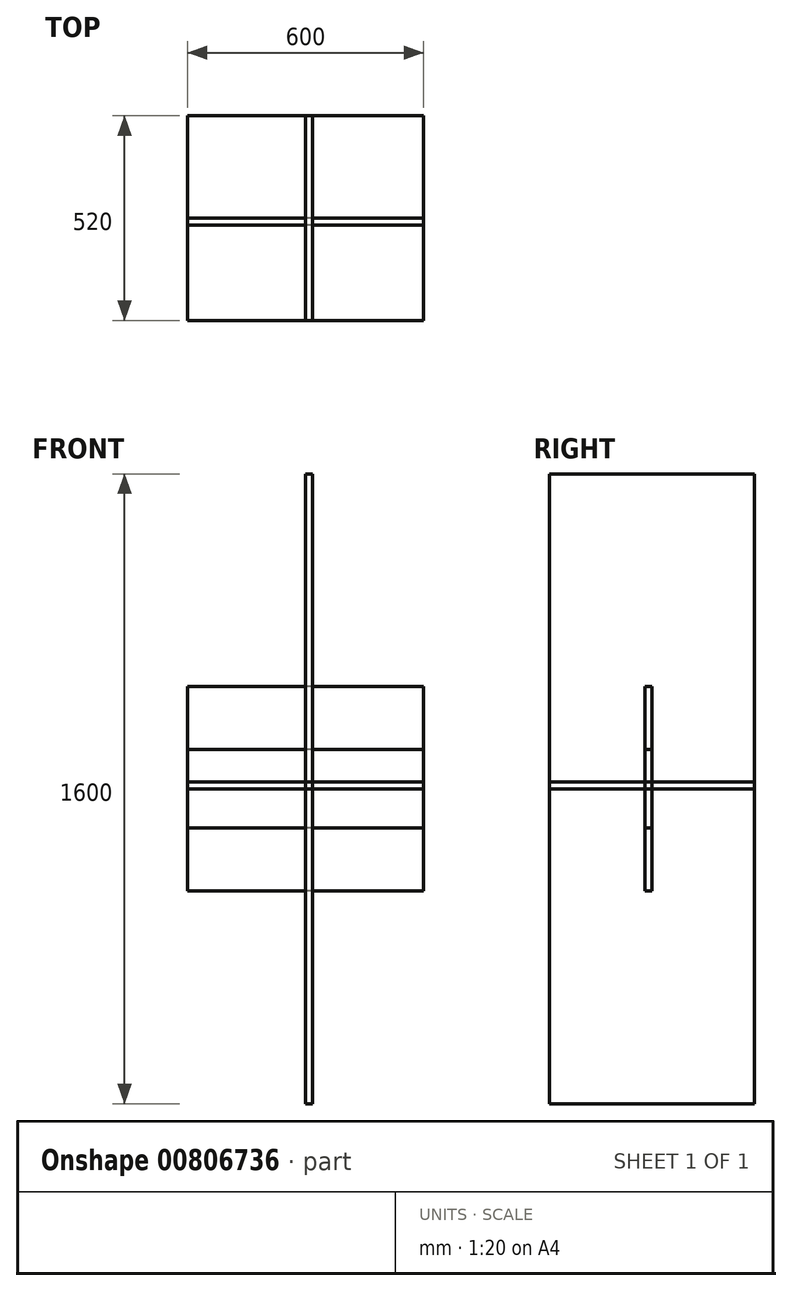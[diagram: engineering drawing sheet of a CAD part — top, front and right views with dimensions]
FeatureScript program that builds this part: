
annotation { "Feature Type Name" : "Feature", "Feature Type Description" : "" }
export const myFeature = defineFeature(function(context is Context, id is Id, definition is map)
    precondition{}
    {
        {
            var Q0;
            Q0=qCreatedBy(makeId("Right.planeOp"),FACE);
            var sketch = newSketch(context, id + "F0", { "sketchPlane" : qUnion([Q0])});
            skLineSegment(sketch, "E0.bottom", {"start": v(260, 800) * mm, "end": v(-260, 800) * mm});
            skLineSegment(sketch, "E0.top", {"start": v(260, -800) * mm, "end": v(-260, -800) * mm});
            skLineSegment(sketch, "E0.left", {"start": v(260, 800) * mm, "end": v(260, -800) * mm});
            skLineSegment(sketch, "E0.right", {"start": v(-260, 800) * mm, "end": v(-260, -800) * mm});
            skPoint(sketch, "E0.middle", {"position": v(0, 0) * mm});
            skSolve(sketch);
        }
        {
            var Q0;
            Q0 = qSketchRegion(id + "F0", true);
            extrude(context, id + "F1", {"entities" : qUnion([Q0]), "depth" : 18 * mm, "offsetDistance" : 25 * mm});
        }
        {
            var Q0;
            Q0=qCreatedBy(makeId("Top.planeOp"),FACE);
            var sketch = newSketch(context, id + "F2", { "sketchPlane" : qUnion([Q0])});
            skLineSegment(sketch, "E1.bottom", {"start": v(300, 260) * mm, "end": v(-300, 260) * mm});
            skLineSegment(sketch, "E1.top", {"start": v(300, -260) * mm, "end": v(-300, -260) * mm});
            skLineSegment(sketch, "E1.left", {"start": v(300, 260) * mm, "end": v(300, -260) * mm});
            skLineSegment(sketch, "E1.right", {"start": v(-300, 260) * mm, "end": v(-300, -260) * mm});
            skPoint(sketch, "E1.middle", {"position": v(0, 0) * mm});
            skSolve(sketch);
        }
        {
            var Q0;
            Q0 = qSketchRegion(id + "F2", true);
            extrude(context, id + "F3", {"entities" : qUnion([Q0]), "depth" : 18 * mm, "offsetDistance" : 25 * mm});
        }
        {
            var Q0;
            Q0=qCreatedBy(makeId("Front.planeOp"),FACE);
            var sketch = newSketch(context, id + "F4", { "sketchPlane" : qUnion([Q0])});
            skLineSegment(sketch, "E2.bottom", {"start": v(300, 260) * mm, "end": v(-300, 260) * mm});
            skLineSegment(sketch, "E2.top", {"start": v(300, -260) * mm, "end": v(-300, -260) * mm});
            skLineSegment(sketch, "E2.left", {"start": v(300, 260) * mm, "end": v(300, -260) * mm});
            skLineSegment(sketch, "E2.right", {"start": v(-300, 260) * mm, "end": v(-300, -260) * mm});
            skPoint(sketch, "E2.middle", {"position": v(0, 0) * mm});
            skSolve(sketch);
        }
        {
            var Q0;
            Q0 = qSketchRegion(id + "F4", true);
            extrude(context, id + "F5", {"entities" : qUnion([Q0]), "depth" : 18 * mm, "offsetDistance" : 25 * mm});
        }
        {
            var Q0;
            Q0=qCreatedBy(makeId("Front.planeOp"),FACE);
            var sketch = newSketch(context, id + "F6", { "sketchPlane" : qUnion([Q0])});
            skLineSegment(sketch, "E3.bottom", {"start": v(300, 100) * mm, "end": v(-300, 100) * mm});
            skLineSegment(sketch, "E3.top", {"start": v(300, -100) * mm, "end": v(-300, -100) * mm});
            skLineSegment(sketch, "E3.left", {"start": v(300, 100) * mm, "end": v(300, -100) * mm});
            skLineSegment(sketch, "E3.right", {"start": v(-300, 100) * mm, "end": v(-300, -100) * mm});
            skPoint(sketch, "E3.middle", {"position": v(0, 0) * mm});
            skSolve(sketch);
        }
        {
            var Q0;
            Q0 = qSketchRegion(id + "F6", true);
            extrude(context, id + "F7", {"entities" : qUnion([Q0]), "depth" : 18 * mm, "offsetDistance" : 25 * mm});
        }
        {
            var Q0;
            Q0=qCreatedBy(makeId("Top.planeOp"),FACE);
            var sketch = newSketch(context, id + "F8", { "sketchPlane" : qUnion([Q0])});
            skLineSegment(sketch, "E4.bottom", {"start": v(300, 260) * mm, "end": v(-300, 260) * mm});
            skLineSegment(sketch, "E4.top", {"start": v(300, -260) * mm, "end": v(-300, -260) * mm});
            skLineSegment(sketch, "E4.left", {"start": v(300, 260) * mm, "end": v(300, -260) * mm});
            skLineSegment(sketch, "E4.right", {"start": v(-300, 260) * mm, "end": v(-300, -260) * mm});
            skPoint(sketch, "E4.middle", {"position": v(0, 0) * mm});
            skSolve(sketch);
        }
        {
            var Q0;
            Q0 = qSketchRegion(id + "F8", true);
            extrude(context, id + "F9", {"entities" : qUnion([Q0]), "depth" : 18 * mm, "offsetDistance" : 25 * mm});
        }
        {
            var Q0;
            Q0=qCreatedBy(makeId("Front.planeOp"),FACE);
            var sketch = newSketch(context, id + "F10", { "sketchPlane" : qUnion([Q0])});
            skLineSegment(sketch, "E5.bottom", {"start": v(300, 260) * mm, "end": v(-300, 260) * mm});
            skLineSegment(sketch, "E5.top", {"start": v(300, -260) * mm, "end": v(-300, -260) * mm});
            skLineSegment(sketch, "E5.left", {"start": v(300, 260) * mm, "end": v(300, -260) * mm});
            skLineSegment(sketch, "E5.right", {"start": v(-300, 260) * mm, "end": v(-300, -260) * mm});
            skPoint(sketch, "E5.middle", {"position": v(0, 0) * mm});
            skSolve(sketch);
        }
        {
            var Q0;
            Q0 = qSketchRegion(id + "F10", true);
            extrude(context, id + "F11", {"entities" : qUnion([Q0]), "depth" : 18 * mm, "offsetDistance" : 25 * mm});
        }
    });
